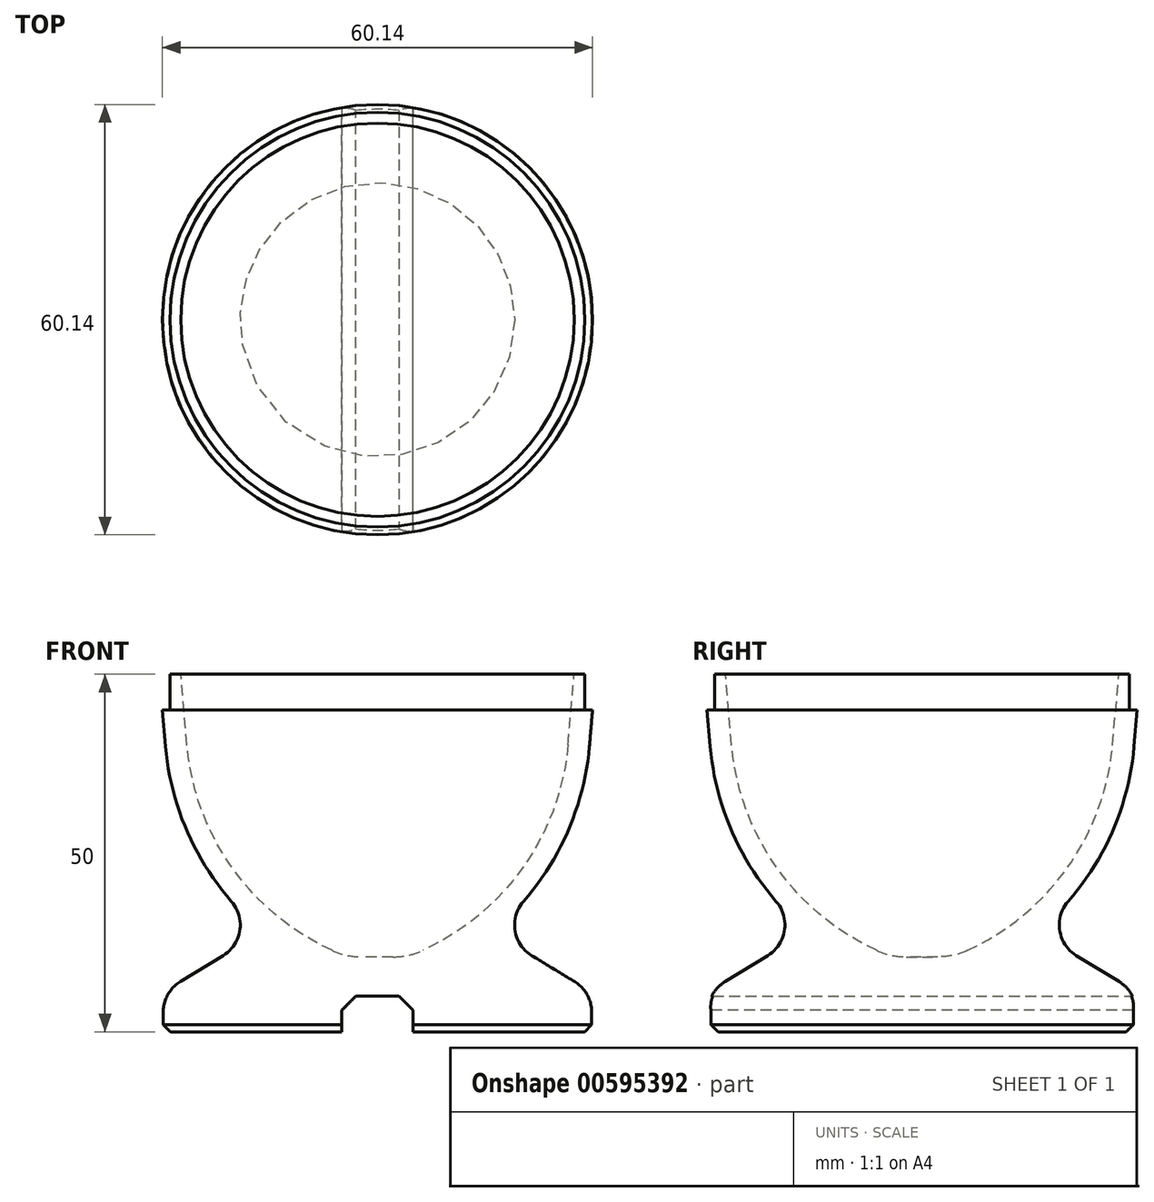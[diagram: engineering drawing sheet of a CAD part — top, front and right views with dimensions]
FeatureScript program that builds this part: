
annotation { "Feature Type Name" : "Feature", "Feature Type Description" : "" }
export const myFeature = defineFeature(function(context is Context, id is Id, definition is map)
    precondition{}
    {
        {
            var Q0;
            Q0=qCreatedBy(makeId("Front.planeOp"),FACE);
            var sketch = newSketch(context, id + "F0", { "sketchPlane" : qUnion([Q0])});
            skLineSegment(sketch, "E0", {"start": v(-26.64, 25.15) * mm, "end": v(-27.5, 35) * mm});
            skArc(sketch, "E1", {"start": v(-26.64, 25.15) * mm, "mid": v(-20.37, 8.03) * mm, "end": v(-6.35, -3.62) * mm});
            skLineSegment(sketch, "E2", {"start": v(-29.95, -12.26) * mm, "end": v(-29.95, -14) * mm});
            skLineSegment(sketch, "E3", {"start": v(-28.95, -15) * mm, "end": v(0, -15) * mm});
            skLineSegment(sketch, "E4.0", {"start": v(-29.63, 24.89) * mm, "end": v(-30.07, 30) * mm});
            skArc(sketch, "E4.1", {"start": v(-29.63, 24.89) * mm, "mid": v(-26.74, 13.32) * mm, "end": v(-20.4, 3.22) * mm});
            skLineSegment(sketch, "E5", {"start": v(-27.5, 35) * mm, "end": v(-29, 35) * mm});
            skPoint(sketch, "E6.visualSharp", {"position": v(-12.5, 0) * mm});
            skLineSegment(sketch, "E7", {"start": v(-29, 35) * mm, "end": v(-29, 30) * mm});
            skLineSegment(sketch, "E8", {"start": v(-29, 30) * mm, "end": v(-30.07, 30) * mm});
            skPoint(sketch, "E9.orphan", {"position": v(-30.51, 35) * mm});
            skPoint(sketch, "E10.visualSharp", {"position": v(-14.64, -2.14) * mm});
            skArc(sketch, "E10.filletArc", {"start": v(-21.57, -4.33) * mm, "mid": v(-19.23, -0.83) * mm, "end": v(-20.4, 3.22) * mm});
            skLineSegment(sketch, "E11", {"start": v(-21.57, -4.33) * mm, "end": v(-27.56, -8) * mm});
            skPoint(sketch, "E12.visualSharp", {"position": v(-29.95, -9.45) * mm});
            skArc(sketch, "E12.filletArc", {"start": v(-27.56, -8) * mm, "mid": v(-29.31, -9.81) * mm, "end": v(-29.95, -12.26) * mm});
            skLineSegment(sketch, "E13", {"start": v(-28.95, -15) * mm, "end": v(-29.95, -14) * mm});
            skLineSegment(sketch, "E14", {"start": v(-2.18, -4.53) * mm, "end": v(0, -4.53) * mm});
            skPoint(sketch, "E15.visualSharp", {"position": v(-4.18, -4.53) * mm});
            skArc(sketch, "E15.filletArc", {"start": v(-6.35, -3.62) * mm, "mid": v(-4.32, -4.3) * mm, "end": v(-2.18, -4.53) * mm});
            skLineSegment(sketch, "E16", {"start": v(-24.95, -14) * mm, "end": v(-29.95, -14) * mm});
            skLineSegment(sketch, "E17", {"start": v(0, -4.53) * mm, "end": v(0, -15) * mm});
            skSolve(sketch);
        }
        {
            var Q0;
            Q0 = qSketchRegion(id + "F0", true);
            var Q1;
            Q1=sQuery(id+"F0.wireOp",EDGE,"E17");
            revolve(context, id + "F1", {"entities" : qUnion([Q0]), "axis" : qUnion([Q1]), "revolveType" : RevolveType.FULL});
        }
        {
            var Q0;
            Q0=qCreatedBy(makeId("Front.planeOp"),FACE);
            var sketch = newSketch(context, id + "F2", { "sketchPlane" : qUnion([Q0])});
            skLineSegment(sketch, "E18.bottom", {"start": v(-5, -10) * mm, "end": v(5, -10) * mm});
            skLineSegment(sketch, "E18.top", {"start": v(-5, -20.68) * mm, "end": v(5, -20.68) * mm});
            skLineSegment(sketch, "E18.left", {"start": v(-5, -10) * mm, "end": v(-5, -20.68) * mm});
            skLineSegment(sketch, "E18.right", {"start": v(5, -10) * mm, "end": v(5, -20.68) * mm});
            skPoint(sketch, "E18.middle", {"position": v(0, -16.53) * mm});
            skSolve(sketch);
        }
        {
            var Q0;
            Q0=makeQuery(id+"F2.imprint","IMPRINT",FACE,{"disambiguationData":[TD([[makeQuery(id+"F2.imprint","IMPRINT",EDGE,{"derivedFrom":sQuery(id+"F2.wireOp",EDGE,"E18.bottom")}),-1.0]])]});
            extrude(context, id + "F3", {"entities" : qUnion([Q0]), "operationType" : NewBodyOperationType.REMOVE, "endBound" : BoundingType.SYMMETRIC, "oppositeDirection" : true, "depth" : 81 * mm, "offsetDistance" : 25 * mm});
        }
        {
            var Q0;
            Q0=makeQuery(id+"F3.boolean.opBoolean","COPY",EDGE,{"derivedFrom":makeQuery(id+"F3.opExtrude","SWEPT_EDGE",EDGE,{"disambiguationData":[OSD([sQuery(id+"F2.wireOp",EDGE,"E18.bottom"),sQuery(id+"F2.wireOp",EDGE,"E18.left")])]})});
            var Q1;
            Q1=makeQuery(id+"F3.boolean.opBoolean","COPY",EDGE,{"derivedFrom":makeQuery(id+"F3.opExtrude","SWEPT_EDGE",EDGE,{"disambiguationData":[OSD([sQuery(id+"F2.wireOp",EDGE,"E18.bottom"),sQuery(id+"F2.wireOp",EDGE,"E18.right")])]})});
            chamfer(context, id + "F4", {"entities" : qUnion([Q0, Q1]), "width" : 2 * mm, "tangentPropagation" : true});
        }
    });
